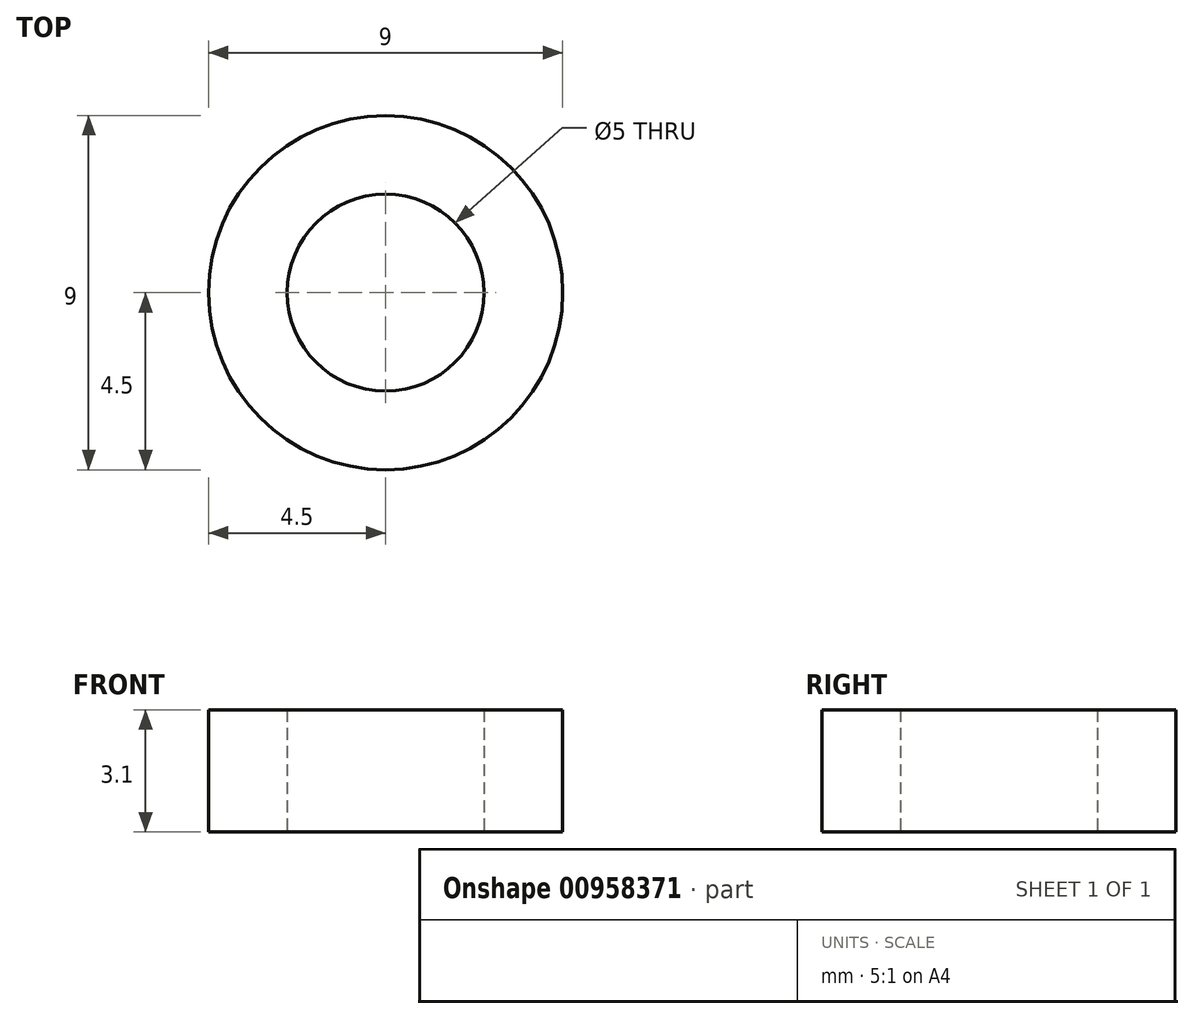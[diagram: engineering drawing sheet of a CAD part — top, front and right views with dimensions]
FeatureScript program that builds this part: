
annotation { "Feature Type Name" : "Feature", "Feature Type Description" : "" }
export const myFeature = defineFeature(function(context is Context, id is Id, definition is map)
    precondition{}
    {
        {
            var Q0;
            Q0=qCreatedBy(makeId("Top.planeOp"),FACE);
            var sketch = newSketch(context, id + "F0", { "sketchPlane" : qUnion([Q0])});
            skCircle(sketch, "E0", {"center": v(0, 0) * mm, "radius": 4.5 * mm});
            skCircle(sketch, "E1", {"center": v(0, 0) * mm, "radius": 2.5 * mm});
            skSolve(sketch);
        }
        {
            var Q0;
            Q0 = qSketchRegion(id + "F0", true);
            extrude(context, id + "F1", {"entities" : qUnion([Q0]), "depth" : 3.1 * mm, "offsetDistance" : 25 * mm});
        }
    });
